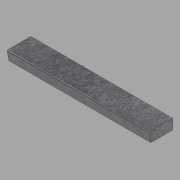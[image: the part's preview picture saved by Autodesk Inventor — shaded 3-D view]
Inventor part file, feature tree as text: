
AUTODESK INVENTOR PART (.ipt)
format: ipt  version: 2022.1 (Build 261234020, 234B)  size: 108,032 bytes
history: native  units: in
note: dims shown in document units (in); Inventor stores cm internally (conversion verified against a paired STEP export)
features: other x3, extrude x1, sketch x1
ambient origin geometry x8: Origin, YZ Plane, XZ Plane, XY Plane, X Axis, Y Axis, Z Axis, Center Point
bodies: Solid1 (feature_tree)
feature tree (5):
  other  "Blocks"
  extrude  "Extrusion1"  Depth=84.125in TaperAngle=0.0deg
  sketch  "Sketch1"  dims[d0=13.0in d1=6.0in d2=13.5in d3=0.5in d4=0.5in d5=84.125in d6=0.0in]
  other  "Profile"
  other  "Profile:1"
